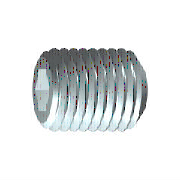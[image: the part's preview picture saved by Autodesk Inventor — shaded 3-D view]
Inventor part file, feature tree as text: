
AUTODESK INVENTOR PART (.ipt)
format: ipt  version: 2019 (Build 230136000, 136)  size: 165,376 bytes
history: native  units: mm (DEFAULTED — no unit token found)
features: sketch x2, extrude x1, other x1, plane x1
ambient origin geometry x8: Origin, YZ Plane, XZ Plane, XY Plane, X Axis, Y Axis, Z Axis, Center Point
bodies: Solid1 (feature_tree), Body (feature_tree)
feature tree (5):
  extrude  "Slot"  TaperAngle=60.0deg  [1 undecoded]
  other  "Work Axis1"
  plane  "Work Plane1"
  sketch  "Sketch1"  dims[d0=1.8mm d1=60.0deg]
  sketch  "Sketch2"  dims[d2=4.0mm d3=2.309401mm d6=90.0deg d4=0.0mm d5=4.0mm d7=0.429415mm d8=45.0deg d21=10.0mm d9=0.0mm d11=4.0mm d12=0.0mm d13=0.429415mm d14=45.0deg d15=0.0mm d29=0.429415mm d30=0.429415mm d31=0.0mm]
note: 1 required parameter value undecoded (feature->parameter linkage not recoverable at this tier; creation-order binding heuristic only, values carry confidence <= 0.55)
